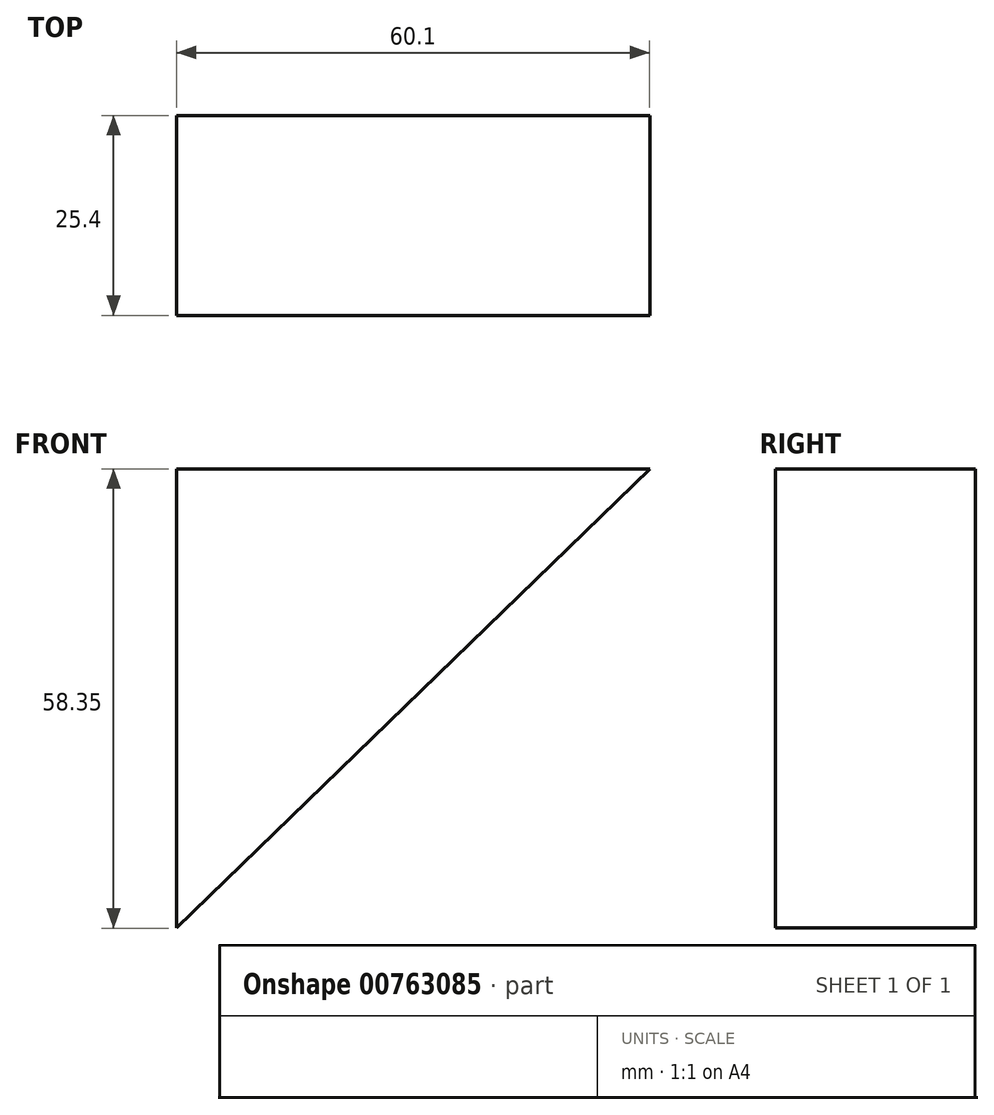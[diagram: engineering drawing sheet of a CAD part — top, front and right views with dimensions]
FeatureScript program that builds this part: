
annotation { "Feature Type Name" : "Feature", "Feature Type Description" : "" }
export const myFeature = defineFeature(function(context is Context, id is Id, definition is map)
    precondition{}
    {
        {
            var Q0;
            Q0=qCreatedBy(makeId("Front.planeOp"),FACE);
            var sketch = newSketch(context, id + "F0", { "sketchPlane" : qUnion([Q0])});
            skLineSegment(sketch, "E0", {"start": v(-26.78, -28.25) * mm, "end": v(-26.78, 30.1) * mm});
            skLineSegment(sketch, "E1", {"start": v(-26.78, 30.1) * mm, "end": v(33.32, 30.1) * mm});
            skLineSegment(sketch, "E2", {"start": v(33.32, 30.1) * mm, "end": v(-26.78, -28.25) * mm});
            skSolve(sketch);
        }
        {
            var Q0;
            Q0=makeQuery(id+"F0.imprint","IMPRINT",FACE,{"disambiguationData":[TD([[makeQuery(id+"F0.imprint","IMPRINT",EDGE,{"derivedFrom":sQuery(id+"F0.wireOp",EDGE,"E0")}),-1.0]])]});
            extrude(context, id + "F1", {"entities" : qUnion([Q0]), "depth" : 25.4 * mm, "offsetDistance" : 25.4 * mm});
        }
    });
